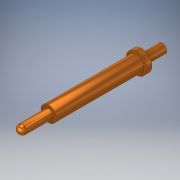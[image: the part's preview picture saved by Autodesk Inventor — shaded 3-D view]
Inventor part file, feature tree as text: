
AUTODESK INVENTOR PART (.ipt)
format: ipt  version: 2019 (Build 230136000, 136)  size: 119,808 bytes
history: native  units: mm
features: extrude x4, sketch x4, fillet x1
ambient origin geometry x8: Origin, YZ Plane, XZ Plane, XY Plane, X Axis, Y Axis, Z Axis, Center Point
bodies: Volumenkörper1 (feature_tree)
feature tree (9):
  extrude  "Extrusion1"  Depth=0.5mm TaperAngle=0.0deg
  extrude  "Extrusion2"  Depth=8.5mm TaperAngle=0.0deg
  extrude  "Extrusion3"  Depth=0.45mm TaperAngle=0.0deg
  fillet  "Rundung1"  Radius=0.45mm
  extrude  "Extrusion4"  Depth=2.0mm TaperAngle=0.0deg
  sketch  "Skizze1"  dims[d0=2.0mm d1=0.5mm d2=0.0mm]
  sketch  "Skizze2"  dims[d3=1.5mm d4=8.5mm d5=0.0mm]
  sketch  "Skizze3"  dims[d6=0.9mm d7=3.0mm d8=0.0mm d9=0.45mm]
  sketch  "Skizze4"  dims[d10=0.9mm d11=2.0mm d12=0.0mm]
